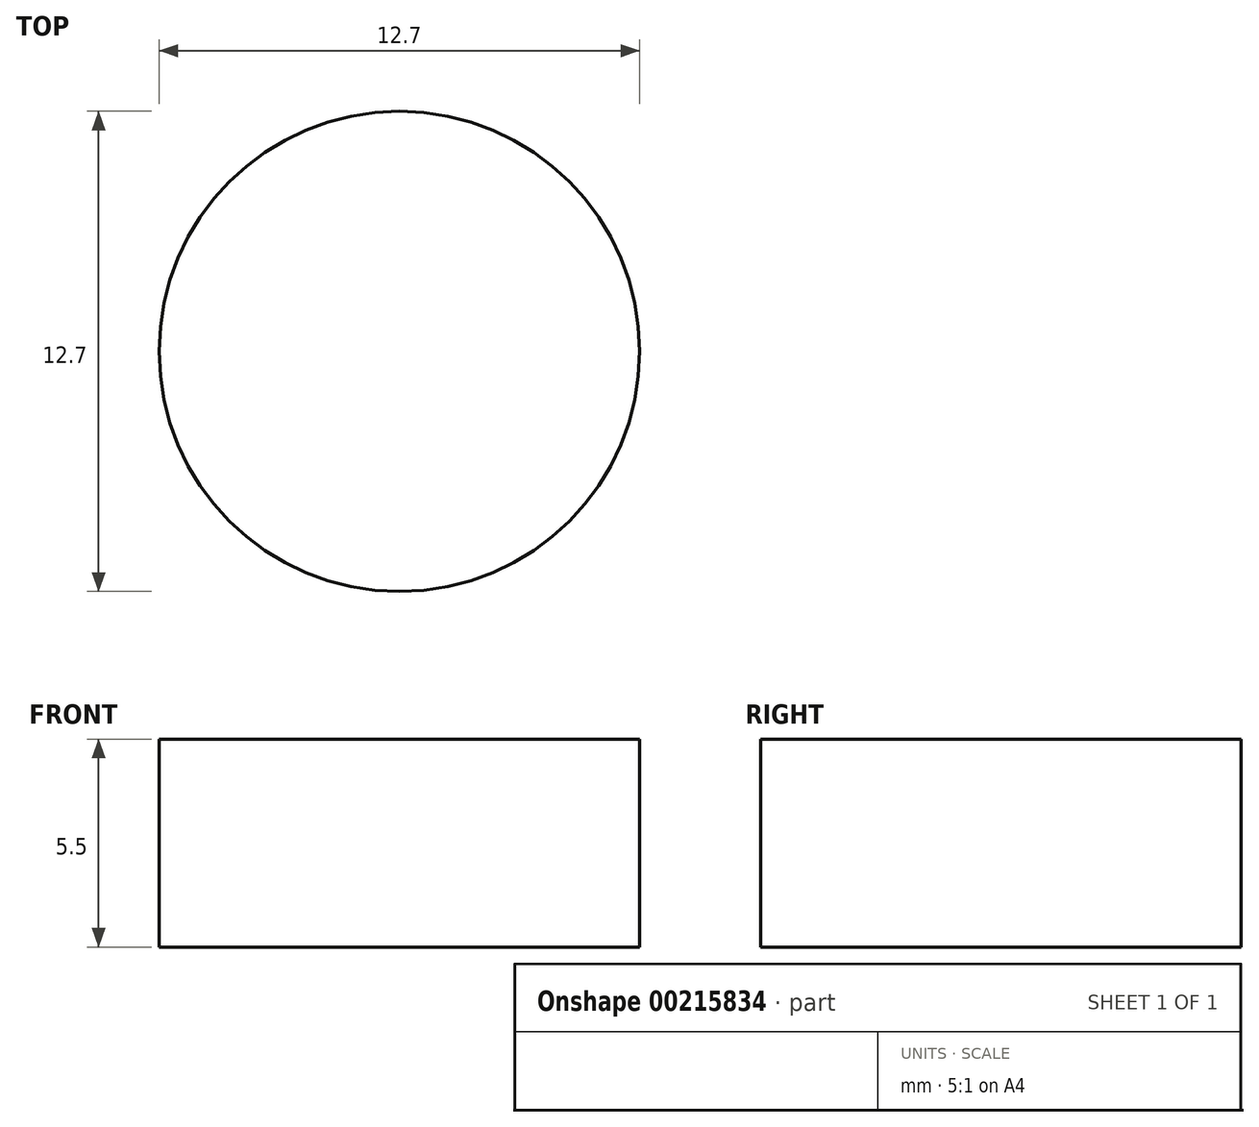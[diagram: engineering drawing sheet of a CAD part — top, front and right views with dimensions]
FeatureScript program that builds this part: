
annotation { "Feature Type Name" : "Feature", "Feature Type Description" : "" }
export const myFeature = defineFeature(function(context is Context, id is Id, definition is map)
    precondition{}
    {
        {
            var Q0;
            Q0=qCreatedBy(makeId("Top.planeOp"),FACE);
            var sketch = newSketch(context, id + "F0", { "sketchPlane" : qUnion([Q0])});
            skCircle(sketch, "E0", {"center": v(0, 0) * mm, "radius": 6.35 * mm});
            skSolve(sketch);
        }
        {
            var Q0;
            Q0=qSketchRegion(id+"F0",true);
            extrude(context, id + "F1", {"entities" : qUnion([Q0]), "depth" : (2 * (2.75)) * mm});
        }
    });
